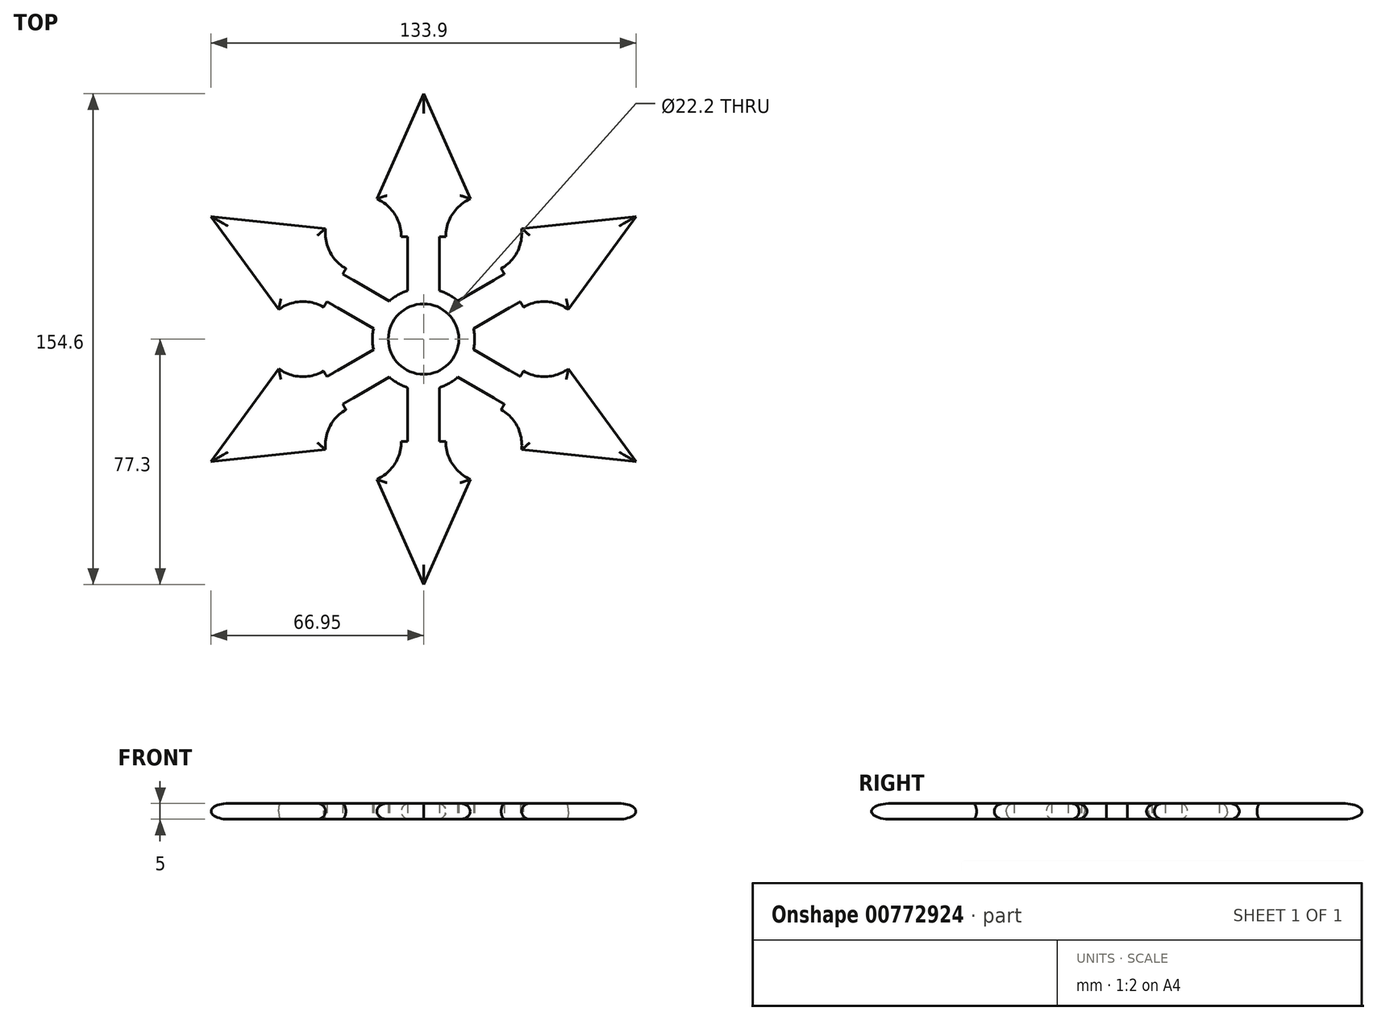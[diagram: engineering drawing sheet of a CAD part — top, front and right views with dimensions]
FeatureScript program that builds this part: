
annotation { "Feature Type Name" : "Feature", "Feature Type Description" : "" }
export const myFeature = defineFeature(function(context is Context, id is Id, definition is map)
    precondition{}
    {
        {
            var Q0;
            Q0=qCreatedBy(makeId("Top.planeOp"),FACE);
            var sketch = newSketch(context, id + "F0", { "sketchPlane" : qUnion([Q0])});
            skCircle(sketch, "E0", {"center": v(0, 0) * mm, "radius": 11.1 * mm});
            skCircle(sketch, "E1", {"center": v(0, 0) * mm, "radius": 16.1 * mm});
            skLineSegment(sketch, "E2", {"start": v(0, 0) * mm, "end": v(0, 32.3) * mm});
            skLineSegment(sketch, "E3", {"start": v(0, 32.3) * mm, "end": v(5, 32.3) * mm});
            skLineSegment(sketch, "E4", {"start": v(0, 32.3) * mm, "end": v(-5, 32.3) * mm});
            skLineSegment(sketch, "E5", {"start": v(-5, 32.3) * mm, "end": v(-5, 15.3) * mm});
            skLineSegment(sketch, "E6", {"start": v(5, 32.3) * mm, "end": v(5, 15.3) * mm});
            skLineSegment(sketch, "E7", {"start": v(0, 32.3) * mm, "end": v(-7, 32.3) * mm});
            skLineSegment(sketch, "E8", {"start": v(0, 32.3) * mm, "end": v(7, 32.3) * mm});
            skPoint(sketch, "E8.endSnap0", {"position": v(2.5, 32.3) * mm});
            skLineSegment(sketch, "E9", {"start": v(0, 32.3) * mm, "end": v(0, 77.3) * mm});
            skLineSegment(sketch, "E10", {"start": v(0, 77.3) * mm, "end": v(-14.72, 44.18) * mm});
            skLineSegment(sketch, "E11", {"start": v(0, 77.3) * mm, "end": v(14.72, 44.18) * mm});
            skPoint(sketch, "E12.visualSharp", {"position": v(-20, 32.3) * mm});
            skPoint(sketch, "E13.visualSharp", {"position": v(20, 32.3) * mm});
            skArc(sketch, "E14", {"start": v(-7, 32.3) * mm, "mid": v(-9.1, 39.39) * mm, "end": v(-14.72, 44.18) * mm});
            skArc(sketch, "E15", {"start": v(14.72, 44.18) * mm, "mid": v(9.1, 39.39) * mm, "end": v(7, 32.3) * mm});
            skLineSegment(sketch, "E16.1.0", {"start": v(-25.48, 20.48) * mm, "end": v(-10.75, 11.98) * mm});
            skLineSegment(sketch, "E16.1.1", {"start": v(0, 0) * mm, "end": v(-27.98, 16.15) * mm});
            skLineSegment(sketch, "E16.1.2", {"start": v(-30.48, 11.82) * mm, "end": v(-15.75, 3.32) * mm});
            skLineSegment(sketch, "E16.1.3", {"start": v(-27.98, 16.15) * mm, "end": v(-31.48, 10.09) * mm});
            skLineSegment(sketch, "E16.1.4", {"start": v(-27.98, 16.15) * mm, "end": v(-24.48, 22.21) * mm});
            skLineSegment(sketch, "E16.1.5", {"start": v(-27.98, 16.15) * mm, "end": v(-66.95, 38.65) * mm});
            skLineSegment(sketch, "E16.1.6", {"start": v(-66.95, 38.65) * mm, "end": v(-30.9, 34.84) * mm});
            skLineSegment(sketch, "E16.1.7", {"start": v(-66.95, 38.65) * mm, "end": v(-45.62, 9.34) * mm});
            skArc(sketch, "E16.1.8", {"start": v(-31.48, 10.09) * mm, "mid": v(-38.66, 11.81) * mm, "end": v(-45.62, 9.34) * mm});
            skArc(sketch, "E16.1.9", {"start": v(-30.9, 34.84) * mm, "mid": v(-29.56, 27.57) * mm, "end": v(-24.48, 22.21) * mm});
            skLineSegment(sketch, "E16.2.0", {"start": v(-30.48, -11.82) * mm, "end": v(-15.75, -3.32) * mm});
            skLineSegment(sketch, "E16.2.1", {"start": v(0, 0) * mm, "end": v(-27.98, -16.15) * mm});
            skLineSegment(sketch, "E16.2.2", {"start": v(-25.48, -20.48) * mm, "end": v(-10.75, -11.98) * mm});
            skLineSegment(sketch, "E16.2.3", {"start": v(-27.98, -16.15) * mm, "end": v(-24.48, -22.21) * mm});
            skLineSegment(sketch, "E16.2.4", {"start": v(-27.98, -16.15) * mm, "end": v(-31.48, -10.09) * mm});
            skLineSegment(sketch, "E16.2.5", {"start": v(-27.98, -16.15) * mm, "end": v(-66.95, -38.65) * mm});
            skLineSegment(sketch, "E16.2.6", {"start": v(-66.95, -38.65) * mm, "end": v(-45.62, -9.34) * mm});
            skLineSegment(sketch, "E16.2.7", {"start": v(-66.95, -38.65) * mm, "end": v(-30.9, -34.84) * mm});
            skArc(sketch, "E16.2.8", {"start": v(-24.48, -22.21) * mm, "mid": v(-29.56, -27.57) * mm, "end": v(-30.9, -34.84) * mm});
            skArc(sketch, "E16.2.9", {"start": v(-45.62, -9.34) * mm, "mid": v(-38.66, -11.81) * mm, "end": v(-31.48, -10.09) * mm});
            skLineSegment(sketch, "E16.3.0", {"start": v(-5, -32.3) * mm, "end": v(-5, -15.3) * mm});
            skLineSegment(sketch, "E16.3.1", {"start": v(0, 0) * mm, "end": v(0, -32.3) * mm});
            skLineSegment(sketch, "E16.3.2", {"start": v(5, -32.3) * mm, "end": v(5, -15.3) * mm});
            skLineSegment(sketch, "E16.3.3", {"start": v(0, -32.3) * mm, "end": v(7, -32.3) * mm});
            skLineSegment(sketch, "E16.3.4", {"start": v(0, -32.3) * mm, "end": v(-7, -32.3) * mm});
            skLineSegment(sketch, "E16.3.5", {"start": v(0, -32.3) * mm, "end": v(0, -77.3) * mm});
            skLineSegment(sketch, "E16.3.6", {"start": v(0, -77.3) * mm, "end": v(-14.72, -44.18) * mm});
            skLineSegment(sketch, "E16.3.7", {"start": v(0, -77.3) * mm, "end": v(14.72, -44.18) * mm});
            skArc(sketch, "E16.3.8", {"start": v(7, -32.3) * mm, "mid": v(9.1, -39.39) * mm, "end": v(14.72, -44.18) * mm});
            skArc(sketch, "E16.3.9", {"start": v(-14.72, -44.18) * mm, "mid": v(-9.1, -39.39) * mm, "end": v(-7, -32.3) * mm});
            skLineSegment(sketch, "E16.4.0", {"start": v(25.48, -20.48) * mm, "end": v(10.75, -11.98) * mm});
            skLineSegment(sketch, "E16.4.1", {"start": v(0, 0) * mm, "end": v(27.98, -16.15) * mm});
            skLineSegment(sketch, "E16.4.2", {"start": v(30.48, -11.82) * mm, "end": v(15.75, -3.32) * mm});
            skLineSegment(sketch, "E16.4.3", {"start": v(27.98, -16.15) * mm, "end": v(31.48, -10.09) * mm});
            skLineSegment(sketch, "E16.4.4", {"start": v(27.98, -16.15) * mm, "end": v(24.48, -22.21) * mm});
            skLineSegment(sketch, "E16.4.5", {"start": v(27.98, -16.15) * mm, "end": v(66.95, -38.65) * mm});
            skLineSegment(sketch, "E16.4.6", {"start": v(66.95, -38.65) * mm, "end": v(30.9, -34.84) * mm});
            skLineSegment(sketch, "E16.4.7", {"start": v(66.95, -38.65) * mm, "end": v(45.62, -9.34) * mm});
            skArc(sketch, "E16.4.8", {"start": v(31.48, -10.09) * mm, "mid": v(38.66, -11.81) * mm, "end": v(45.62, -9.34) * mm});
            skArc(sketch, "E16.4.9", {"start": v(30.9, -34.84) * mm, "mid": v(29.56, -27.57) * mm, "end": v(24.48, -22.21) * mm});
            skLineSegment(sketch, "E16.5.0", {"start": v(30.48, 11.82) * mm, "end": v(15.75, 3.32) * mm});
            skLineSegment(sketch, "E16.5.1", {"start": v(0, 0) * mm, "end": v(27.98, 16.15) * mm});
            skLineSegment(sketch, "E16.5.2", {"start": v(25.48, 20.48) * mm, "end": v(10.75, 11.98) * mm});
            skLineSegment(sketch, "E16.5.3", {"start": v(27.98, 16.15) * mm, "end": v(24.48, 22.21) * mm});
            skLineSegment(sketch, "E16.5.4", {"start": v(27.98, 16.15) * mm, "end": v(31.48, 10.09) * mm});
            skLineSegment(sketch, "E16.5.5", {"start": v(27.98, 16.15) * mm, "end": v(66.95, 38.65) * mm});
            skLineSegment(sketch, "E16.5.6", {"start": v(66.95, 38.65) * mm, "end": v(45.62, 9.34) * mm});
            skLineSegment(sketch, "E16.5.7", {"start": v(66.95, 38.65) * mm, "end": v(30.9, 34.84) * mm});
            skArc(sketch, "E16.5.8", {"start": v(24.48, 22.21) * mm, "mid": v(29.56, 27.57) * mm, "end": v(30.9, 34.84) * mm});
            skArc(sketch, "E16.5.9", {"start": v(45.62, 9.34) * mm, "mid": v(38.66, 11.81) * mm, "end": v(31.48, 10.09) * mm});
            skSolve(sketch);
        }
        {
            var Q0;
            {var subQ0=sQuery(id+"F0.wireOp",EDGE,"E16.1.0");Q0=makeQuery(id+"F0.imprint","IMPRINT",FACE,{"disambiguationData":[TD([[makeQuery(id+"F0.imprint","IMPRINT",EDGE,{"derivedFrom":subQ0}),-1.0]])]});}
            var Q1;
            {var subQ0=sQuery(id+"F0.wireOp",EDGE,"E16.1.2");Q1=makeQuery(id+"F0.imprint","IMPRINT",FACE,{"disambiguationData":[TD([[makeQuery(id+"F0.imprint","IMPRINT",EDGE,{"derivedFrom":subQ0}),1.0]])]});}
            var Q2;
            {var subQ5=sQuery(id+"F0.wireOp",EDGE,"E16.1.1");var subQ7=sQuery(id+"F0.wireOp",EDGE,"E0");var subQ8=makeQuery(id+"F0.imprint","INTERSECT",VERTEX,{"derivedFrom":[subQ7,subQ5]});Q2=makeQuery(id+"F0.imprint","IMPRINT",FACE,{"disambiguationData":[TD([[makeQuery(id+"F0.imprint","IMPRINT",EDGE,{"disambiguationData":[TD([[subQ8,-1.0]])],"derivedFrom":subQ7}),-1.0]])]});}
            var Q3;
            {var subQ4=sQuery(id+"F0.wireOp",EDGE,"E2");var subQ5=sQuery(id+"F0.wireOp",EDGE,"E0");var subQ6=makeQuery(id+"F0.imprint","INTERSECT",VERTEX,{"derivedFrom":[subQ5,subQ4]});Q3=makeQuery(id+"F0.imprint","IMPRINT",FACE,{"disambiguationData":[TD([[makeQuery(id+"F0.imprint","IMPRINT",EDGE,{"disambiguationData":[TD([[subQ6,-1.0]])],"derivedFrom":subQ5}),-1.0]])]});}
            var Q4;
            {var subQ2=sQuery(id+"F0.wireOp",EDGE,"E2");var subQ6=sQuery(id+"F0.wireOp",EDGE,"E0");var subQ9=makeQuery(id+"F0.imprint","INTERSECT",VERTEX,{"derivedFrom":[subQ6,subQ2]});Q4=makeQuery(id+"F0.imprint","IMPRINT",FACE,{"disambiguationData":[TD([[makeQuery(id+"F0.imprint","IMPRINT",EDGE,{"disambiguationData":[TD([[subQ9,1.0]])],"derivedFrom":subQ6}),-1.0]])]});}
            var Q5;
            {var subQ5=sQuery(id+"F0.wireOp",EDGE,"E16.5.1");var subQ7=sQuery(id+"F0.wireOp",EDGE,"E0");var subQ8=makeQuery(id+"F0.imprint","INTERSECT",VERTEX,{"derivedFrom":[subQ7,subQ5]});Q5=makeQuery(id+"F0.imprint","IMPRINT",FACE,{"disambiguationData":[TD([[makeQuery(id+"F0.imprint","IMPRINT",EDGE,{"disambiguationData":[TD([[subQ8,1.0]])],"derivedFrom":subQ7}),-1.0]])]});}
            var Q6;
            {var subQ5=sQuery(id+"F0.wireOp",EDGE,"E16.3.1");var subQ7=sQuery(id+"F0.wireOp",EDGE,"E0");var subQ8=makeQuery(id+"F0.imprint","INTERSECT",VERTEX,{"derivedFrom":[subQ7,subQ5]});Q6=makeQuery(id+"F0.imprint","IMPRINT",FACE,{"disambiguationData":[TD([[makeQuery(id+"F0.imprint","IMPRINT",EDGE,{"disambiguationData":[TD([[subQ8,-1.0]])],"derivedFrom":subQ7}),-1.0]])]});}
            var Q7;
            {var subQ3=sQuery(id+"F0.wireOp",EDGE,"E16.2.1");var subQ7=sQuery(id+"F0.wireOp",EDGE,"E0");var subQ8=makeQuery(id+"F0.imprint","INTERSECT",VERTEX,{"derivedFrom":[subQ7,subQ3]});Q7=makeQuery(id+"F0.imprint","IMPRINT",FACE,{"disambiguationData":[TD([[makeQuery(id+"F0.imprint","IMPRINT",EDGE,{"disambiguationData":[TD([[subQ8,-1.0]])],"derivedFrom":subQ7}),-1.0]])]});}
            var Q8;
            {var subQ0=sQuery(id+"F0.wireOp",EDGE,"E16.2.2");Q8=makeQuery(id+"F0.imprint","IMPRINT",FACE,{"disambiguationData":[TD([[makeQuery(id+"F0.imprint","IMPRINT",EDGE,{"derivedFrom":subQ0}),1.0]])]});}
            var Q9;
            {var subQ0=sQuery(id+"F0.wireOp",EDGE,"E16.2.0");Q9=makeQuery(id+"F0.imprint","IMPRINT",FACE,{"disambiguationData":[TD([[makeQuery(id+"F0.imprint","IMPRINT",EDGE,{"derivedFrom":subQ0}),-1.0]])]});}
            var Q10;
            {var subQ0=sQuery(id+"F0.wireOp",EDGE,"E16.5.2");Q10=makeQuery(id+"F0.imprint","IMPRINT",FACE,{"disambiguationData":[TD([[makeQuery(id+"F0.imprint","IMPRINT",EDGE,{"derivedFrom":subQ0}),1.0]])]});}
            var Q11;
            {var subQ0=sQuery(id+"F0.wireOp",EDGE,"E16.5.0");Q11=makeQuery(id+"F0.imprint","IMPRINT",FACE,{"disambiguationData":[TD([[makeQuery(id+"F0.imprint","IMPRINT",EDGE,{"derivedFrom":subQ0}),-1.0]])]});}
            var Q12;
            {var subQ0=sQuery(id+"F0.wireOp",EDGE,"E6");Q12=makeQuery(id+"F0.imprint","IMPRINT",FACE,{"disambiguationData":[TD([[makeQuery(id+"F0.imprint","IMPRINT",EDGE,{"derivedFrom":subQ0}),-1.0]])]});}
            var Q13;
            {var subQ0=sQuery(id+"F0.wireOp",EDGE,"E5");Q13=makeQuery(id+"F0.imprint","IMPRINT",FACE,{"disambiguationData":[TD([[makeQuery(id+"F0.imprint","IMPRINT",EDGE,{"derivedFrom":subQ0}),1.0]])]});}
            var Q14;
            {var subQ0=sQuery(id+"F0.wireOp",EDGE,"E16.4.2");Q14=makeQuery(id+"F0.imprint","IMPRINT",FACE,{"disambiguationData":[TD([[makeQuery(id+"F0.imprint","IMPRINT",EDGE,{"derivedFrom":subQ0}),1.0]])]});}
            var Q15;
            {var subQ0=sQuery(id+"F0.wireOp",EDGE,"E16.4.0");Q15=makeQuery(id+"F0.imprint","IMPRINT",FACE,{"disambiguationData":[TD([[makeQuery(id+"F0.imprint","IMPRINT",EDGE,{"derivedFrom":subQ0}),-1.0]])]});}
            var Q16;
            {var subQ0=sQuery(id+"F0.wireOp",EDGE,"E16.3.2");Q16=makeQuery(id+"F0.imprint","IMPRINT",FACE,{"disambiguationData":[TD([[makeQuery(id+"F0.imprint","IMPRINT",EDGE,{"derivedFrom":subQ0}),1.0]])]});}
            var Q17;
            {var subQ0=sQuery(id+"F0.wireOp",EDGE,"E16.3.0");Q17=makeQuery(id+"F0.imprint","IMPRINT",FACE,{"disambiguationData":[TD([[makeQuery(id+"F0.imprint","IMPRINT",EDGE,{"derivedFrom":subQ0}),-1.0]])]});}
            extrude(context, id + "F1", {"entities" : qUnion([Q0, Q1, Q2, Q3, Q4, Q5, Q6, Q7, Q8, Q9, Q10, Q11, Q12, Q13, Q14, Q15, Q16, Q17]), "depth" : 5 * mm, "offsetDistance" : 25 * mm});
        }
        {
            var Q0;
            {var subQ0=sQuery(id+"F0.wireOp",EDGE,"E16.1.5");Q0=makeQuery(id+"F0.imprint","IMPRINT",FACE,{"disambiguationData":[TD([[makeQuery(id+"F0.imprint","IMPRINT",EDGE,{"derivedFrom":subQ0}),-1.0]])]});}
            var Q1;
            {var subQ0=sQuery(id+"F0.wireOp",EDGE,"E16.1.5");Q1=makeQuery(id+"F0.imprint","IMPRINT",FACE,{"disambiguationData":[TD([[makeQuery(id+"F0.imprint","IMPRINT",EDGE,{"derivedFrom":subQ0}),1.0]])]});}
            var Q2;
            {var subQ0=sQuery(id+"F0.wireOp",EDGE,"E9");Q2=makeQuery(id+"F0.imprint","IMPRINT",FACE,{"disambiguationData":[TD([[makeQuery(id+"F0.imprint","IMPRINT",EDGE,{"derivedFrom":subQ0}),1.0]])]});}
            var Q3;
            {var subQ0=sQuery(id+"F0.wireOp",EDGE,"E9");Q3=makeQuery(id+"F0.imprint","IMPRINT",FACE,{"disambiguationData":[TD([[makeQuery(id+"F0.imprint","IMPRINT",EDGE,{"derivedFrom":subQ0}),-1.0]])]});}
            var Q4;
            {var subQ0=sQuery(id+"F0.wireOp",EDGE,"E16.5.5");Q4=makeQuery(id+"F0.imprint","IMPRINT",FACE,{"disambiguationData":[TD([[makeQuery(id+"F0.imprint","IMPRINT",EDGE,{"derivedFrom":subQ0}),1.0]])]});}
            var Q5;
            {var subQ0=sQuery(id+"F0.wireOp",EDGE,"E16.5.5");Q5=makeQuery(id+"F0.imprint","IMPRINT",FACE,{"disambiguationData":[TD([[makeQuery(id+"F0.imprint","IMPRINT",EDGE,{"derivedFrom":subQ0}),-1.0]])]});}
            var Q6;
            {var subQ0=sQuery(id+"F0.wireOp",EDGE,"E16.4.5");Q6=makeQuery(id+"F0.imprint","IMPRINT",FACE,{"disambiguationData":[TD([[makeQuery(id+"F0.imprint","IMPRINT",EDGE,{"derivedFrom":subQ0}),1.0]])]});}
            var Q7;
            {var subQ0=sQuery(id+"F0.wireOp",EDGE,"E16.4.5");Q7=makeQuery(id+"F0.imprint","IMPRINT",FACE,{"disambiguationData":[TD([[makeQuery(id+"F0.imprint","IMPRINT",EDGE,{"derivedFrom":subQ0}),-1.0]])]});}
            var Q8;
            {var subQ0=sQuery(id+"F0.wireOp",EDGE,"E16.3.5");Q8=makeQuery(id+"F0.imprint","IMPRINT",FACE,{"disambiguationData":[TD([[makeQuery(id+"F0.imprint","IMPRINT",EDGE,{"derivedFrom":subQ0}),1.0]])]});}
            var Q9;
            {var subQ0=sQuery(id+"F0.wireOp",EDGE,"E16.3.5");Q9=makeQuery(id+"F0.imprint","IMPRINT",FACE,{"disambiguationData":[TD([[makeQuery(id+"F0.imprint","IMPRINT",EDGE,{"derivedFrom":subQ0}),-1.0]])]});}
            var Q10;
            {var subQ0=sQuery(id+"F0.wireOp",EDGE,"E16.2.5");Q10=makeQuery(id+"F0.imprint","IMPRINT",FACE,{"disambiguationData":[TD([[makeQuery(id+"F0.imprint","IMPRINT",EDGE,{"derivedFrom":subQ0}),1.0]])]});}
            var Q11;
            {var subQ0=sQuery(id+"F0.wireOp",EDGE,"E16.2.5");Q11=makeQuery(id+"F0.imprint","IMPRINT",FACE,{"disambiguationData":[TD([[makeQuery(id+"F0.imprint","IMPRINT",EDGE,{"derivedFrom":subQ0}),-1.0]])]});}
            extrude(context, id + "F2", {"entities" : qUnion([Q0, Q1, Q2, Q3, Q4, Q5, Q6, Q7, Q8, Q9, Q10, Q11]), "operationType" : NewBodyOperationType.ADD, "depth" : 5 * mm, "offsetDistance" : 25 * mm});
        }
        {
            var Q0;
            Q0=makeQuery(id+"F2.opExtrude","CAP_EDGE",EDGE,{"disambiguationData":[OSD([sQuery(id+"F0.wireOp",EDGE,"E16.2.7")])],"isStart":false});
            var Q1;
            Q1=makeQuery(id+"F2.opExtrude","CAP_EDGE",EDGE,{"disambiguationData":[OSD([sQuery(id+"F0.wireOp",EDGE,"E16.2.6")])],"isStart":false});
            var Q2;
            Q2=makeQuery(id+"F2.opExtrude","CAP_EDGE",EDGE,{"disambiguationData":[OSD([sQuery(id+"F0.wireOp",EDGE,"E16.2.6")])],"isStart":true});
            var Q3;
            Q3=makeQuery(id+"F2.opExtrude","CAP_EDGE",EDGE,{"disambiguationData":[OSD([sQuery(id+"F0.wireOp",EDGE,"E16.3.6")])],"isStart":false});
            var Q4;
            Q4=makeQuery(id+"F2.opExtrude","CAP_EDGE",EDGE,{"disambiguationData":[OSD([sQuery(id+"F0.wireOp",EDGE,"E16.3.7")])],"isStart":false});
            var Q5;
            Q5=makeQuery(id+"F2.opExtrude","CAP_EDGE",EDGE,{"disambiguationData":[OSD([sQuery(id+"F0.wireOp",EDGE,"E16.3.7")])],"isStart":true});
            var Q6;
            Q6=makeQuery(id+"F2.opExtrude","CAP_EDGE",EDGE,{"disambiguationData":[OSD([sQuery(id+"F0.wireOp",EDGE,"E16.3.6")])],"isStart":true});
            var Q7;
            Q7=makeQuery(id+"F2.opExtrude","CAP_EDGE",EDGE,{"disambiguationData":[OSD([sQuery(id+"F0.wireOp",EDGE,"E16.4.7")])],"isStart":false});
            var Q8;
            Q8=makeQuery(id+"F2.opExtrude","CAP_EDGE",EDGE,{"disambiguationData":[OSD([sQuery(id+"F0.wireOp",EDGE,"E16.4.7")])],"isStart":true});
            var Q9;
            Q9=makeQuery(id+"F2.opExtrude","CAP_EDGE",EDGE,{"disambiguationData":[OSD([sQuery(id+"F0.wireOp",EDGE,"E16.4.6")])],"isStart":false});
            var Q10;
            Q10=makeQuery(id+"F2.opExtrude","CAP_EDGE",EDGE,{"disambiguationData":[OSD([sQuery(id+"F0.wireOp",EDGE,"E16.4.6")])],"isStart":true});
            var Q11;
            Q11=makeQuery(id+"F2.opExtrude","CAP_EDGE",EDGE,{"disambiguationData":[OSD([sQuery(id+"F0.wireOp",EDGE,"E16.5.7")])],"isStart":false});
            var Q12;
            Q12=makeQuery(id+"F2.opExtrude","CAP_EDGE",EDGE,{"disambiguationData":[OSD([sQuery(id+"F0.wireOp",EDGE,"E16.5.6")])],"isStart":false});
            var Q13;
            Q13=makeQuery(id+"F2.opExtrude","CAP_EDGE",EDGE,{"disambiguationData":[OSD([sQuery(id+"F0.wireOp",EDGE,"E16.5.7")])],"isStart":true});
            var Q14;
            Q14=makeQuery(id+"F2.opExtrude","CAP_EDGE",EDGE,{"disambiguationData":[OSD([sQuery(id+"F0.wireOp",EDGE,"E16.5.6")])],"isStart":true});
            var Q15;
            Q15=makeQuery(id+"F2.opExtrude","CAP_EDGE",EDGE,{"disambiguationData":[OSD([sQuery(id+"F0.wireOp",EDGE,"E16.1.6")])],"isStart":false});
            var Q16;
            Q16=makeQuery(id+"F2.opExtrude","CAP_EDGE",EDGE,{"disambiguationData":[OSD([sQuery(id+"F0.wireOp",EDGE,"E16.1.7")])],"isStart":false});
            var Q17;
            Q17=makeQuery(id+"F2.opExtrude","CAP_EDGE",EDGE,{"disambiguationData":[OSD([sQuery(id+"F0.wireOp",EDGE,"E10")])],"isStart":false});
            var Q18;
            Q18=makeQuery(id+"F2.opExtrude","CAP_EDGE",EDGE,{"disambiguationData":[OSD([sQuery(id+"F0.wireOp",EDGE,"E11")])],"isStart":false});
            var Q19;
            Q19=makeQuery(id+"F2.opExtrude","CAP_EDGE",EDGE,{"disambiguationData":[OSD([sQuery(id+"F0.wireOp",EDGE,"E10")])],"isStart":true});
            var Q20;
            Q20=makeQuery(id+"F2.opExtrude","CAP_EDGE",EDGE,{"disambiguationData":[OSD([sQuery(id+"F0.wireOp",EDGE,"E11")])],"isStart":true});
            var Q21;
            Q21=makeQuery(id+"F2.opExtrude","CAP_EDGE",EDGE,{"disambiguationData":[OSD([sQuery(id+"F0.wireOp",EDGE,"E16.1.7")])],"isStart":true});
            var Q22;
            Q22=makeQuery(id+"F2.opExtrude","CAP_EDGE",EDGE,{"disambiguationData":[OSD([sQuery(id+"F0.wireOp",EDGE,"E16.1.6")])],"isStart":true});
            var Q23;
            Q23=makeQuery(id+"F2.opExtrude","CAP_EDGE",EDGE,{"disambiguationData":[OSD([sQuery(id+"F0.wireOp",EDGE,"E16.2.7")])],"isStart":true});
            var Q24;
            Q24=makeQuery(id+"F2.opExtrude","CAP_EDGE",EDGE,{"disambiguationData":[OSD([sQuery(id+"F0.wireOp",EDGE,"E16.4.9")])],"isStart":true});
            var Q25;
            Q25=makeQuery(id+"F2.opExtrude","CAP_EDGE",EDGE,{"disambiguationData":[OSD([sQuery(id+"F0.wireOp",EDGE,"E16.4.9")])],"isStart":false});
            var Q26;
            Q26=makeQuery(id+"F2.opExtrude","CAP_EDGE",EDGE,{"disambiguationData":[OSD([sQuery(id+"F0.wireOp",EDGE,"E16.4.8")])],"isStart":true});
            var Q27;
            Q27=makeQuery(id+"F2.opExtrude","CAP_EDGE",EDGE,{"disambiguationData":[OSD([sQuery(id+"F0.wireOp",EDGE,"E16.4.8")])],"isStart":false});
            var Q28;
            Q28=makeQuery(id+"F2.opExtrude","CAP_EDGE",EDGE,{"disambiguationData":[OSD([sQuery(id+"F0.wireOp",EDGE,"E16.5.9")])],"isStart":false});
            var Q29;
            Q29=makeQuery(id+"F2.opExtrude","CAP_EDGE",EDGE,{"disambiguationData":[OSD([sQuery(id+"F0.wireOp",EDGE,"E16.5.9")])],"isStart":true});
            var Q30;
            Q30=makeQuery(id+"F2.opExtrude","CAP_EDGE",EDGE,{"disambiguationData":[OSD([sQuery(id+"F0.wireOp",EDGE,"E16.5.8")])],"isStart":false});
            var Q31;
            Q31=makeQuery(id+"F2.opExtrude","CAP_EDGE",EDGE,{"disambiguationData":[OSD([sQuery(id+"F0.wireOp",EDGE,"E16.5.8")])],"isStart":true});
            var Q32;
            Q32=makeQuery(id+"F2.opExtrude","CAP_EDGE",EDGE,{"disambiguationData":[OSD([sQuery(id+"F0.wireOp",EDGE,"E15")])],"isStart":false});
            var Q33;
            Q33=makeQuery(id+"F2.opExtrude","CAP_EDGE",EDGE,{"disambiguationData":[OSD([sQuery(id+"F0.wireOp",EDGE,"E15")])],"isStart":true});
            var Q34;
            Q34=makeQuery(id+"F2.opExtrude","CAP_EDGE",EDGE,{"disambiguationData":[OSD([sQuery(id+"F0.wireOp",EDGE,"E14")])],"isStart":true});
            var Q35;
            Q35=makeQuery(id+"F2.opExtrude","CAP_EDGE",EDGE,{"disambiguationData":[OSD([sQuery(id+"F0.wireOp",EDGE,"E14")])],"isStart":false});
            var Q36;
            Q36=makeQuery(id+"F2.opExtrude","CAP_EDGE",EDGE,{"disambiguationData":[OSD([sQuery(id+"F0.wireOp",EDGE,"E16.1.9")])],"isStart":true});
            var Q37;
            Q37=makeQuery(id+"F2.opExtrude","CAP_EDGE",EDGE,{"disambiguationData":[OSD([sQuery(id+"F0.wireOp",EDGE,"E16.1.9")])],"isStart":false});
            var Q38;
            Q38=makeQuery(id+"F2.opExtrude","CAP_EDGE",EDGE,{"disambiguationData":[OSD([sQuery(id+"F0.wireOp",EDGE,"E16.1.8")])],"isStart":false});
            var Q39;
            Q39=makeQuery(id+"F2.opExtrude","CAP_EDGE",EDGE,{"disambiguationData":[OSD([sQuery(id+"F0.wireOp",EDGE,"E16.1.8")])],"isStart":true});
            var Q40;
            Q40=makeQuery(id+"F2.opExtrude","CAP_EDGE",EDGE,{"disambiguationData":[OSD([sQuery(id+"F0.wireOp",EDGE,"E16.2.9")])],"isStart":false});
            var Q41;
            Q41=makeQuery(id+"F2.opExtrude","CAP_EDGE",EDGE,{"disambiguationData":[OSD([sQuery(id+"F0.wireOp",EDGE,"E16.2.9")])],"isStart":true});
            var Q42;
            Q42=makeQuery(id+"F2.opExtrude","CAP_EDGE",EDGE,{"disambiguationData":[OSD([sQuery(id+"F0.wireOp",EDGE,"E16.2.8")])],"isStart":false});
            var Q43;
            Q43=makeQuery(id+"F2.opExtrude","CAP_EDGE",EDGE,{"disambiguationData":[OSD([sQuery(id+"F0.wireOp",EDGE,"E16.2.8")])],"isStart":true});
            var Q44;
            Q44=makeQuery(id+"F2.opExtrude","CAP_EDGE",EDGE,{"disambiguationData":[OSD([sQuery(id+"F0.wireOp",EDGE,"E16.3.8")])],"isStart":false});
            var Q45;
            Q45=makeQuery(id+"F2.opExtrude","CAP_EDGE",EDGE,{"disambiguationData":[OSD([sQuery(id+"F0.wireOp",EDGE,"E16.3.8")])],"isStart":true});
            var Q46;
            Q46=makeQuery(id+"F2.opExtrude","CAP_EDGE",EDGE,{"disambiguationData":[OSD([sQuery(id+"F0.wireOp",EDGE,"E16.3.9")])],"isStart":false});
            var Q47;
            Q47=makeQuery(id+"F2.opExtrude","CAP_EDGE",EDGE,{"disambiguationData":[OSD([sQuery(id+"F0.wireOp",EDGE,"E16.3.9")])],"isStart":true});
            fillet(context, id + "F3", {"entities" : qUnion([Q0, Q1, Q2, Q3, Q4, Q5, Q6, Q7, Q8, Q9, Q10, Q11, Q12, Q13, Q14, Q15, Q16, Q17, Q18, Q19, Q20, Q21, Q22, Q23, Q24, Q25, Q26, Q27, Q28, Q29, Q30, Q31, Q32, Q33, Q34, Q35, Q36, Q37, Q38, Q39, Q40, Q41, Q42, Q43, Q44, Q45, Q46, Q47]), "radius" : 2.5 * mm, "tangentPropagation" : true, "allowEdgeOverflow" : false});
        }
    });
